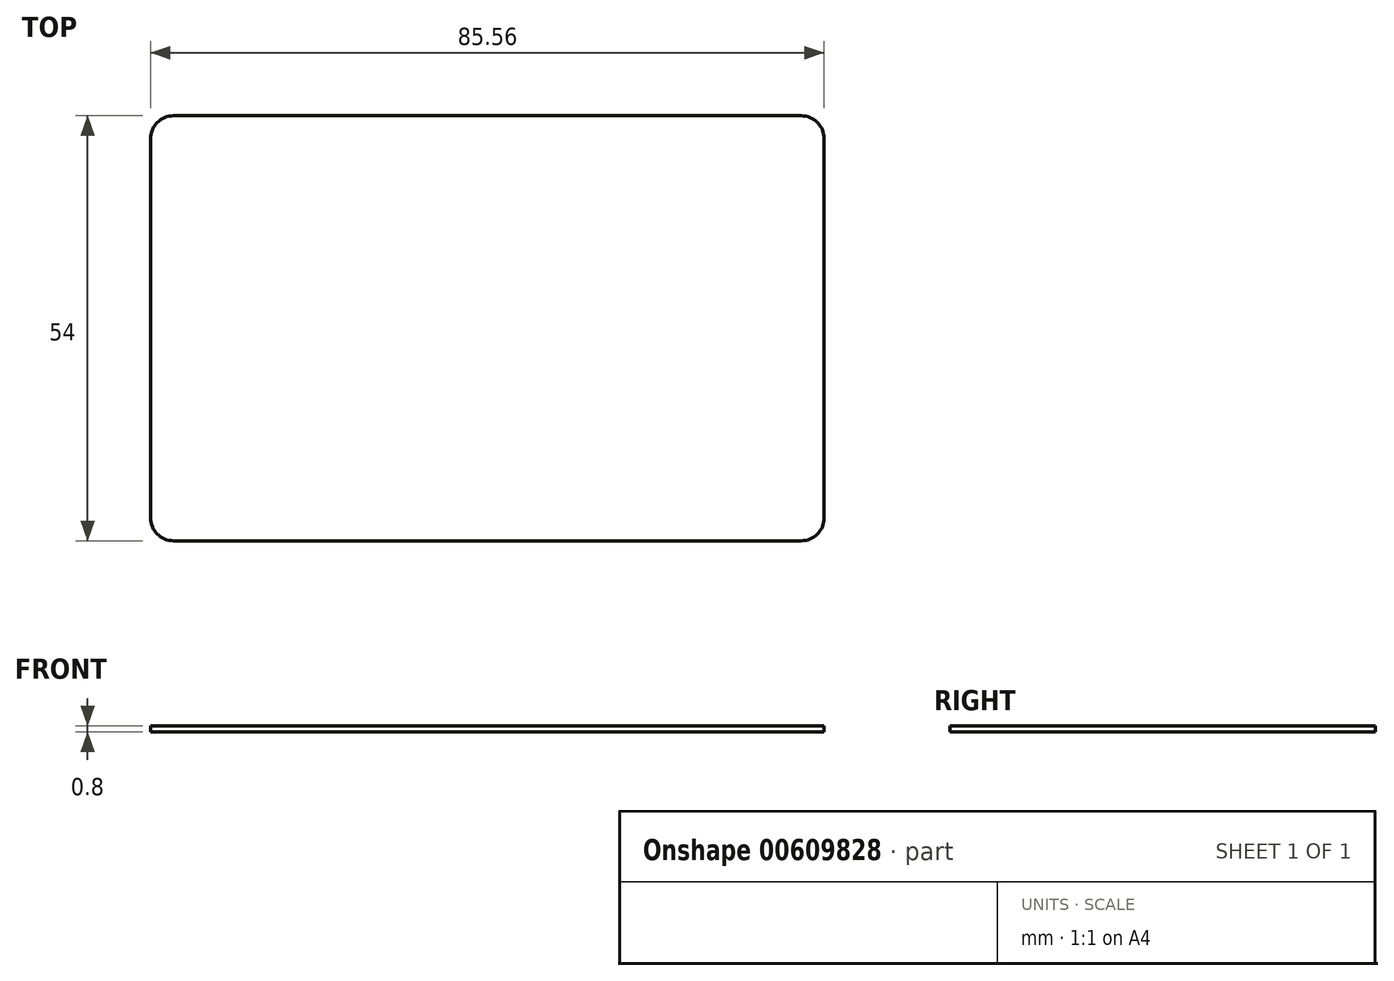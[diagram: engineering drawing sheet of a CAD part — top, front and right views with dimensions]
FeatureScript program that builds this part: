
annotation { "Feature Type Name" : "Feature", "Feature Type Description" : "" }
export const myFeature = defineFeature(function(context is Context, id is Id, definition is map)
    precondition{}
    {
        {
            var Q0;
            Q0=qCreatedBy(makeId("Top.planeOp"),FACE);
            var sketch = newSketch(context, id + "F0", { "sketchPlane" : qUnion([Q0])});
            skLineSegment(sketch, "E0.bottom", {"start": v(-39.86, 27) * mm, "end": v(39.86, 27) * mm});
            skLineSegment(sketch, "E0.top", {"start": v(-39.86, -27) * mm, "end": v(39.86, -27) * mm});
            skLineSegment(sketch, "E0.left", {"start": v(-42.78, 24.08) * mm, "end": v(-42.78, -24.08) * mm});
            skLineSegment(sketch, "E0.right", {"start": v(42.78, 24.08) * mm, "end": v(42.78, -24.08) * mm});
            skPoint(sketch, "E0.middle", {"position": v(0, 0) * mm});
            skPoint(sketch, "E1.visualSharp", {"position": v(-42.78, 27) * mm});
            skArc(sketch, "E1.filletArc", {"start": v(-39.86, 27) * mm, "mid": v(-41.92, 26.14) * mm, "end": v(-42.78, 24.08) * mm});
            skPoint(sketch, "E2.visualSharp", {"position": v(-42.78, -27) * mm});
            skArc(sketch, "E2.filletArc", {"start": v(-42.78, -24.08) * mm, "mid": v(-41.92, -26.14) * mm, "end": v(-39.86, -27) * mm});
            skPoint(sketch, "E3.visualSharp", {"position": v(42.78, -27) * mm});
            skArc(sketch, "E3.filletArc", {"start": v(39.86, -27) * mm, "mid": v(41.92, -26.14) * mm, "end": v(42.78, -24.08) * mm});
            skPoint(sketch, "E4.visualSharp", {"position": v(42.78, 27) * mm});
            skArc(sketch, "E4.filletArc", {"start": v(42.78, 24.08) * mm, "mid": v(41.92, 26.14) * mm, "end": v(39.86, 27) * mm});
            skSolve(sketch);
        }
        {
            var Q0;
            Q0 = qSketchRegion(id + "F0", true);
            extrude(context, id + "F1", {"entities" : qUnion([Q0]), "depth" : 0.8 * mm, "offsetDistance" : 25.4 * mm});
        }
    });
